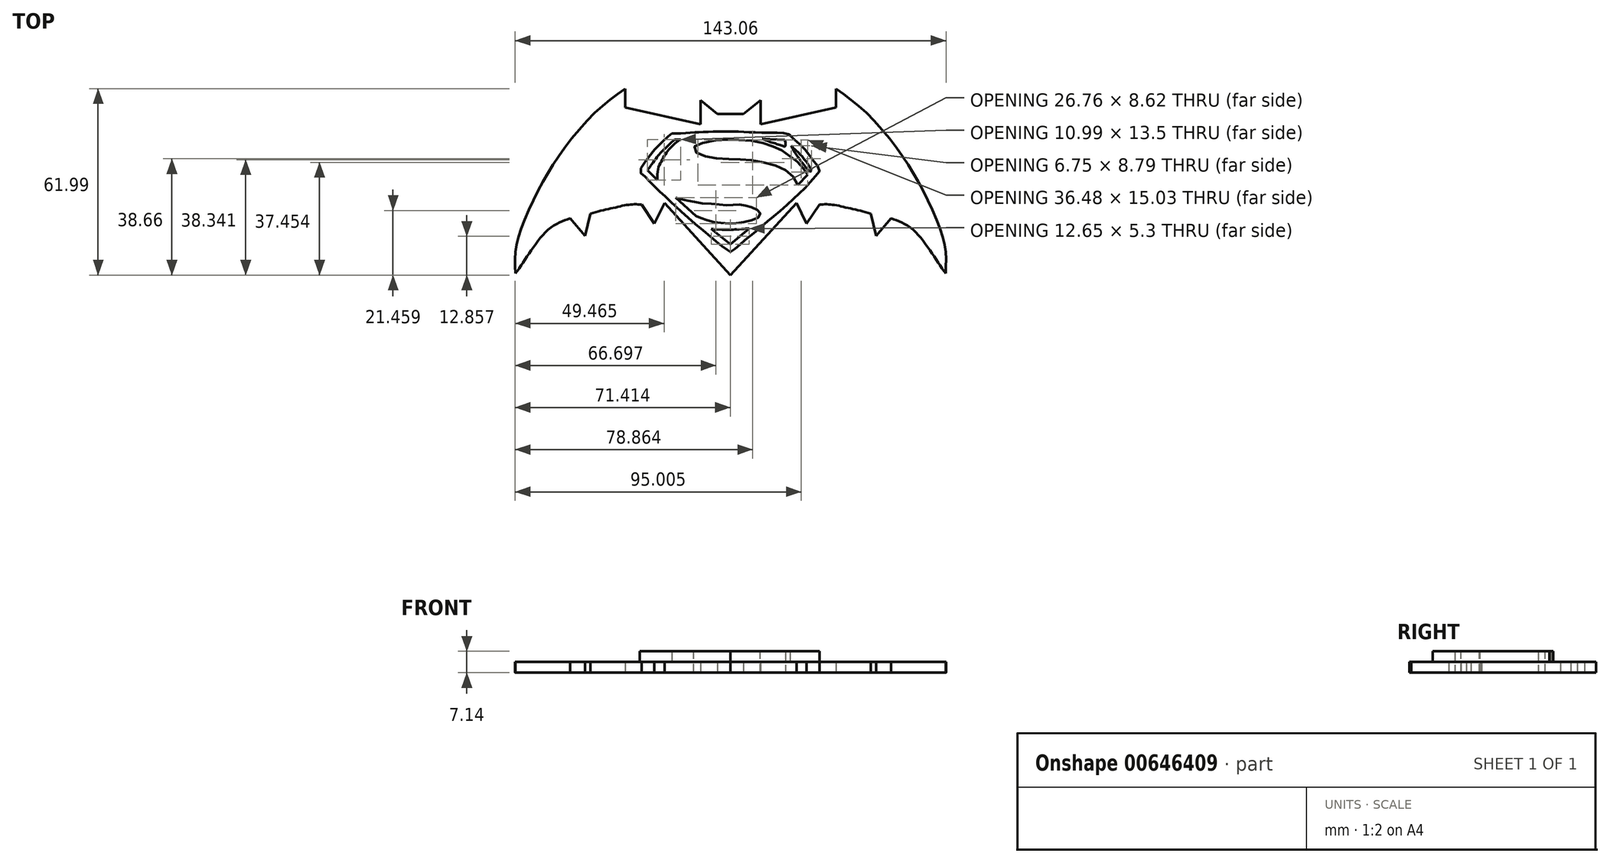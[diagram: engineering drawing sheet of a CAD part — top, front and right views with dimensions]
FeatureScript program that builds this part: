
annotation { "Feature Type Name" : "Feature", "Feature Type Description" : "" }
export const myFeature = defineFeature(function(context is Context, id is Id, definition is map)
    precondition{}
    {
        {
            var Q0;
            Q0=qCreatedBy(makeId("Top.planeOp"),FACE);
            var sketch = newSketch(context, id + "F0", { "sketchPlane" : qUnion([Q0])});
            skLineSegment(sketch, "E0", {"start": v(0, -29.29) * mm, "end": v(-21.94, -5.3) * mm});
            skLineSegment(sketch, "E1", {"start": v(-21.94, -5.3) * mm, "end": v(-25.27, -12.15) * mm});
            skLineSegment(sketch, "E2", {"start": v(-25.27, -12.15) * mm, "end": v(-29.54, -5.84) * mm});
            skFitSpline(sketch, "E3", {"points": [v(-29.54, -5.84) * mm, v(-33.44, -5.84) * mm, v(-39.05, -6.98) * mm, v(-46.5, -8.89) * mm], "startDerivative": vector(-13.8, 0.93) * mm, "endDerivative": vector(-19.94, -6.94) * mm});
            skLineSegment(sketch, "E4", {"start": v(-46.5, -8.89) * mm, "end": v(-48.35, -16.27) * mm});
            skLineSegment(sketch, "E5", {"start": v(-48.35, -16.27) * mm, "end": v(-53.26, -10.46) * mm});
            skFitSpline(sketch, "E6", {"points": [v(-53.26, -10.46) * mm, v(-56.7, -11.7) * mm, v(-60.93, -14.52) * mm, v(-65.15, -19.53) * mm, v(-68.59, -24.69) * mm, v(-71.4, -28.75) * mm], "startDerivative": vector(-20.24, -6.27) * mm, "endDerivative": vector(-14.3, -20.24) * mm});
            skFitSpline(sketch, "E7", {"points": [v(-71.4, -28.75) * mm, v(-71.4, -21.87) * mm, v(-69.37, -13.43) * mm, v(-63.27, 0) * mm, v(-56.23, 11.43) * mm, v(-44.98, 24.73) * mm, v(-34.97, 32.7) * mm], "startDerivative": vector(-2.55, 54.29) * mm, "endDerivative": vector(57.68, 41.15) * mm});
            skLineSegment(sketch, "E8", {"start": v(-34.97, 32.7) * mm, "end": v(-34.97, 26.45) * mm});
            skLineSegment(sketch, "E9", {"start": v(-34.97, 26.45) * mm, "end": v(-9.95, 20.82) * mm});
            skLineSegment(sketch, "E10", {"start": v(-9.95, 20.82) * mm, "end": v(-9.95, 28.8) * mm});
            skLineSegment(sketch, "E11", {"start": v(-9.95, 28.8) * mm, "end": v(-4.32, 24.26) * mm});
            skLineSegment(sketch, "E12", {"start": v(-4.32, 24.26) * mm, "end": v(0, 24.26) * mm});
            skLineSegment(sketch, "E13.MirrorCS", {"start": v(4.32, 24.26) * mm, "end": v(0, 24.26) * mm});
            skLineSegment(sketch, "E14.MirrorCS", {"start": v(9.95, 28.8) * mm, "end": v(4.32, 24.26) * mm});
            skLineSegment(sketch, "E15.MirrorCS", {"start": v(9.95, 20.82) * mm, "end": v(9.95, 28.8) * mm});
            skLineSegment(sketch, "E16.MirrorCS", {"start": v(34.97, 26.45) * mm, "end": v(9.95, 20.82) * mm});
            skLineSegment(sketch, "E17.MirrorCS", {"start": v(34.97, 32.7) * mm, "end": v(34.97, 26.45) * mm});
            skFitSpline(sketch, "E18.MirrorCS", {"points": [v(71.4, -28.75) * mm, v(71.4, -21.87) * mm, v(69.37, -13.43) * mm, v(63.27, 0) * mm, v(56.23, 11.43) * mm, v(44.98, 24.73) * mm, v(34.97, 32.7) * mm], "startDerivative": vector(2.55, 54.29) * mm, "endDerivative": vector(-57.68, 41.15) * mm});
            skFitSpline(sketch, "E19.MirrorCS", {"points": [v(53.26, -10.46) * mm, v(56.7, -11.7) * mm, v(60.93, -14.52) * mm, v(65.15, -19.53) * mm, v(68.59, -24.69) * mm, v(71.4, -28.75) * mm], "startDerivative": vector(20.24, -6.27) * mm, "endDerivative": vector(14.3, -20.24) * mm});
            skLineSegment(sketch, "E20.MirrorCS", {"start": v(48.35, -16.27) * mm, "end": v(53.26, -10.46) * mm});
            skLineSegment(sketch, "E21.MirrorCS", {"start": v(46.5, -8.89) * mm, "end": v(48.35, -16.27) * mm});
            skFitSpline(sketch, "E22.MirrorCS", {"points": [v(29.54, -5.84) * mm, v(33.44, -5.84) * mm, v(39.05, -6.98) * mm, v(46.5, -8.89) * mm], "startDerivative": vector(13.8, 0.93) * mm, "endDerivative": vector(19.94, -6.94) * mm});
            skLineSegment(sketch, "E23.MirrorCS", {"start": v(25.27, -12.15) * mm, "end": v(29.54, -5.84) * mm});
            skLineSegment(sketch, "E24.MirrorCS", {"start": v(21.94, -5.3) * mm, "end": v(25.27, -12.15) * mm});
            skLineSegment(sketch, "E25.MirrorCS", {"start": v(0, -29.29) * mm, "end": v(21.94, -5.3) * mm});
            skFitSpline(sketch, "E26", {"points": [v(-6.44, -13.95) * mm, v(-5.68, -14) * mm, v(-4.34, -14.09) * mm, v(-2.2, -14.18) * mm, v(0, -14.17) * mm, v(2.5, -14.06) * mm, v(5.6, -13.82) * mm, v(6.2, -13.78) * mm], "startDerivative": vector(7.48, -0.48) * mm, "endDerivative": vector(5.5, 0.3) * mm});
            skLineSegment(sketch, "E27", {"start": v(-6.44, -13.95) * mm, "end": v(0, -19.08) * mm});
            skLineSegment(sketch, "E28", {"start": v(0, -19.08) * mm, "end": v(6.2, -13.78) * mm});
            skLineSegment(sketch, "E29", {"start": v(-18.21, -3.52) * mm, "end": v(-11.46, -9.7) * mm});
            skFitSpline(sketch, "E30", {"points": [v(-11.46, -9.7) * mm, v(-10.56, -10.1) * mm, v(-8.56, -10.77) * mm, v(-6.1, -11.55) * mm, v(-3.86, -11.88) * mm, v(-0.33, -12.15) * mm, v(1.86, -12.1) * mm, v(5, -11.58) * mm, v(8.21, -10.65) * mm, v(9.66, -9.7) * mm, v(9.77, -8.65) * mm, v(9.15, -7.83) * mm, v(7.82, -7.04) * mm, v(5.86, -6.44) * mm, v(4.25, -6.01) * mm, v(2.15, -5.88) * mm, v(0, -6) * mm, v(-2.41, -6.01) * mm, v(-5.3, -5.7) * mm, v(-9.23, -5.41) * mm, v(-12.19, -4.88) * mm, v(-14.4, -4.47) * mm, v(-16.82, -3.98) * mm, v(-18.21, -3.52) * mm], "startDerivative": vector(27.77, -13.95) * mm, "endDerivative": vector(-35.91, 13.18) * mm});
            skLineSegment(sketch, "E31", {"start": v(25.58, 4.09) * mm, "end": v(22.35, 0.65) * mm});
            skFitSpline(sketch, "E32", {"points": [v(25.58, 4.09) * mm, v(24.77, 5.23) * mm, v(23.54, 6.93) * mm, v(21.88, 8.58) * mm, v(20.02, 10.03) * mm, v(17.64, 11.77) * mm, v(14.97, 13.08) * mm, v(12.89, 13.97) * mm, v(9.02, 14.95) * mm, v(5.25, 15.5) * mm, v(0.62, 15.67) * mm, v(-2.1, 15.67) * mm, v(-7.57, 15.08) * mm, v(-10.88, 14.1) * mm, v(-12.07, 13.3) * mm, v(-12.07, 12.1) * mm, v(-10.03, 10.7) * mm, v(-7.19, 9.94) * mm, v(-3.41, 9.4) * mm, v(1.09, 9.26) * mm, v(4.27, 9.05) * mm, v(8.05, 8.71) * mm, v(12.46, 7.82) * mm, v(16.28, 6.63) * mm, v(19.04, 5.06) * mm, v(21.16, 3.07) * mm, v(22.35, 0.65) * mm], "startDerivative": vector(-29.55, 41.43) * mm, "endDerivative": vector(27.27, -69.59) * mm});
            skLineSegment(sketch, "E33", {"start": v(-16.57, 15.8) * mm, "end": v(-18.6, 15.8) * mm});
            skFitSpline(sketch, "E34", {"points": [v(-18.6, 15.8) * mm, v(-19.41, 15.04) * mm, v(-21.11, 13.42) * mm, v(-22.72, 11.8) * mm, v(-24.12, 10.28) * mm, v(-26.2, 7.52) * mm, v(-27.56, 5.61) * mm], "startDerivative": vector(-6.15, -5.84) * mm, "endDerivative": vector(-7.3, -10.34) * mm});
            skPoint(sketch, "E35.1.internal.snap0", {"position": v(-17.59, 15.8) * mm});
            skFitSpline(sketch, "E35", {"points": [v(-16.57, 15.8) * mm, v(-17.59, 15.16) * mm, v(-19.5, 13.47) * mm, v(-20.86, 11.94) * mm, v(-22.13, 10.11) * mm, v(-23.19, 8.16) * mm, v(-24.08, 6) * mm, v(-24.34, 2.3) * mm], "startDerivative": vector(-9.04, -4.99) * mm, "endDerivative": vector(-0.07, -21.77) * mm});
            skLineSegment(sketch, "E36", {"start": v(-27.56, 5.61) * mm, "end": v(-24.34, 2.3) * mm});
            skLineSegment(sketch, "E37", {"start": v(10.47, 16.01) * mm, "end": v(17.98, 15.59) * mm});
            skPoint(sketch, "E38.4.internal.snap0", {"position": v(14.22, 15.8) * mm});
            skFitSpline(sketch, "E38", {"points": [v(17.98, 15.59) * mm, v(18.28, 14.14) * mm, v(17.98, 13.47) * mm, v(16.8, 13.85) * mm, v(14.22, 14.61) * mm, v(10.47, 16.01) * mm], "startDerivative": vector(2.6, -8.42) * mm, "endDerivative": vector(-13.23, 5.37) * mm});
            skFitSpline(sketch, "E39", {"points": [v(20.1, 13.76) * mm, v(20.61, 12.7) * mm, v(21.84, 10.66) * mm, v(22.99, 9.18) * mm, v(24.35, 7.31) * mm, v(26.3, 4.98) * mm], "startDerivative": vector(2.89, -6.42) * mm, "endDerivative": vector(8.55, -9.8) * mm});
            skFitSpline(sketch, "E40", {"points": [v(20.1, 13.76) * mm, v(21.29, 12.57) * mm, v(22.94, 11) * mm, v(24.39, 9.3) * mm, v(25.62, 7.7) * mm, v(26.85, 5.61) * mm], "startDerivative": vector(6.3, -6.5) * mm, "endDerivative": vector(5.65, -10.17) * mm});
            skLineSegment(sketch, "E41", {"start": v(26.85, 5.61) * mm, "end": v(26.3, 4.98) * mm});
            skFitSpline(sketch, "E42", {"points": [v(-19.5, 17.75) * mm, v(-16.57, 17.82) * mm, v(-12.84, 18.1) * mm, v(-10.21, 18.23) * mm, v(-6.57, 18.37) * mm, v(-2.93, 18.38) * mm, v(1.24, 18.45) * mm, v(5.69, 18.25) * mm, v(12.23, 18.05) * mm, v(18.9, 17.65) * mm, v(19.7, 17.11) * mm], "startDerivative": vector(31.61, 0.2) * mm, "endDerivative": vector(10.75, -11.7) * mm});
            skFitSpline(sketch, "E43", {"points": [v(19.7, 17.11) * mm, v(22.13, 14.88) * mm, v(25.23, 11.85) * mm, v(27.25, 9.08) * mm, v(29.54, 5.7) * mm, v(27.86, 3.26) * mm, v(24.35, -0.66) * mm, v(20.58, -4.25) * mm, v(15.66, -8.65) * mm, v(11.55, -12.04) * mm, v(7.85, -15.22) * mm, v(4.88, -17.59) * mm, v(2.12, -20.1) * mm, v(0, -21.58) * mm], "startDerivative": vector(33.55, -31.1) * mm, "endDerivative": vector(-34.43, -22) * mm});
            skFitSpline(sketch, "E44", {"points": [v(0, -21.58) * mm, v(-1.12, -20.9) * mm, v(-3.81, -18.95) * mm, v(-7.25, -15.98) * mm, v(-13.24, -10.98) * mm, v(-17.42, -7.2) * mm, v(-20.45, -4.3) * mm, v(-23.48, -1.52) * mm, v(-26.58, 1.45) * mm, v(-28.6, 3.61) * mm, v(-30.09, 5.16) * mm, v(-28.74, 7.73) * mm, v(-26.11, 11.46) * mm, v(-21, 16.6) * mm, v(-19.5, 17.75) * mm], "startDerivative": vector(-23.99, 13.8) * mm, "endDerivative": vector(24.49, 17.4) * mm});
            skSolve(sketch);
        }
        {
            var Q0;
            Q0=makeQuery(id+"F0.imprint","IMPRINT",FACE,{"disambiguationData":[TD([[makeQuery(id+"F0.imprint","IMPRINT",EDGE,{"derivedFrom":sQuery(id+"F0.wireOp",EDGE,"E26")}),1.0]])]});
            extrude(context, id + "F1", {"entities" : qUnion([Q0]), "depth" : 7.14 * mm});
        }
        {
            var Q0;
            Q0=qSketchRegion(id+"F0",true);
            extrude(context, id + "F2", {"entities" : qUnion([Q0]), "operationType" : NewBodyOperationType.ADD, "depth" : 3.56 * mm});
        }
    });
